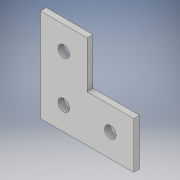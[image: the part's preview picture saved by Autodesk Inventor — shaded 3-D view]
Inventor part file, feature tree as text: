
AUTODESK INVENTOR PART (.ipt)
format: ipt  version: 2018 (Build 220112000, 112)  size: 117,248 bytes
history: native  units: in
note: dims shown in document units (in); Inventor stores cm internally (conversion verified against a paired STEP export)
features: hole x3, extrude x1, sketch x1
ambient origin geometry x8: Origin, YZ Plane, XZ Plane, XY Plane, X Axis, Y Axis, Z Axis, Center Point
bodies: Solid1 (feature_tree), Body1 (feature_tree)
feature tree (5):
  extrude  "Extrusion1"  Depth=1.0in
  hole  "Hole1"  [1 undecoded]
  hole  "Hole2"  [1 undecoded]
  hole  "Hole3"  [1 undecoded]
  sketch  "Sketch1"  dims[d0=1.0in d1=1.0in d2=1.0in d3=0.0in d4=1.0in d5=1.0in d6=0.25in d7=0.75in d8=0.375in d9=0.25in d10=0.5635in d11=1.0in d12=0.8108in d13=1.0in d14=1.0in d15=0.25in d16=0.75in d17=0.375in d18=0.25in d19=0.5635in d20=1.0in d21=0.8108in d22=1.0in d23=1.0in d24=0.25in d25=0.75in d26=0.375in d27=0.25in d28=0.5635in d29=1.0in d30=0.8108in]
note: 3 required parameter values undecoded (feature->parameter linkage not recoverable at this tier; creation-order binding heuristic only, values carry confidence <= 0.55)
